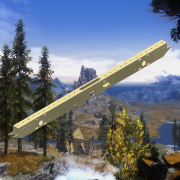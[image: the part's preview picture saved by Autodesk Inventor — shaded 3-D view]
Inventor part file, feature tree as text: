
AUTODESK INVENTOR PART (.ipt)
format: ipt  version: 2015 SP1 (Build 190203100, 203)  size: 1,349,120 bytes
history: native  units: in
note: dims shown in document units (in); Inventor stores cm internally (conversion verified against a paired STEP export)
features: sketch x12, extrude x6, hole x6, reference x6, plane x5, other x2, fillet x1, imported_body x1
ambient origin geometry x8: Origin, YZ Plane, XZ Plane, XY Plane, X Axis, Y Axis, Z Axis, Center Point
bodies: Body1 (feature_tree)
feature tree (39):
  other  "Cut-Extrude2"
  other  "1 x 2 x 0.10 Pre-Drilled Tube Stock (59 length)1"
  plane  "Work Plane2"
  extrude  "Extrusion1"  Depth=99.0in TaperAngle=0.0deg
  extrude  "Extrusion2"  Depth=1.0in
  hole  "Hole1"  [1 undecoded]
  plane  "Work Plane3"
  extrude  "Extrusion3"  TaperAngle=30.0deg  [1 undecoded]
  plane  "Work Plane4"
  extrude  "Extrusion4"  Depth=1.0in
  plane  "Work Plane5"
  extrude  "Extrusion5"  Depth=0.75in
  hole  "Hole2"  [1 undecoded]
  plane  "Work Plane7"
  hole  "Hole3"  [1 undecoded]
  extrude  "Extrusion6"  Depth=4.5in
  hole  "Hole4"  [1 undecoded]
  hole  "Hole5"  [1 undecoded]
  fillet  "Fillet1"  Radius=10.04in
  hole  "Hole6"  [1 undecoded]
  imported_body  "Base1"
  sketch  "Sketch2"  dims[d4=15.5in d5=99.0in d6=0.0in]
  sketch  "Sketch3"  dims[d7=1.0in d8=1.0in]
  sketch  "Sketch4"  dims[d9=30.0deg d10=1.0in]
  sketch  "Sketch5"  dims[d11=1.0in d12=30.0deg]
  sketch  "Sketch6"  dims[d13=1.0in d14=0.0in d16=0.625in]
  sketch  "Sketch7"  dims[d17=15.5in d20=0.75in]
  sketch  "Sketch8"  dims[d21=0.75in]
  sketch  "Sketch10"  dims[d22=0.875in d23=0.75in d24=0.119in d25=0.25in d26=0.563in d27=1.0in d28=0.8108in d29=0.5in]
  sketch  "Sketch11"  dims[d30=3.75in d31=1.0in d32=0.0in]
  sketch  "Sketch12"  dims[d33=0.6in d34=4.5in]
  reference  "Reference1"
  reference  "Reference2"
  sketch  "Sketch13"  dims[d35=1.0in d36=0.0in d37=0.3in]
  reference  "Reference3"
  reference  "Reference4"
  sketch  "Sketch14"  dims[d38=1.0in d39=0.0in d40=10.04in d41=10.04in d42=1.4in d43=0.75in d44=0.375in d45=0.25in d46=0.5635in d47=1.0in d48=0.8108in d49=0.266in d50=0.75in d51=0.507in d52=0.25in d53=0.5635in d54=1.0in d55=0.8108in d56=0.375in d57=0.201in d58=0.201in d59=0.375in d60=0.201in d61=0.375in d62=0.201in d63=0.375in d64=0.201in d65=0.375in d66=0.7874in d68=1.548in d69=0.7874in d71=1.542in d75=1.0in d76=0.0in d77=0.163in d78=0.75in d79=0.507in d80=0.25in d81=0.5635in d82=1.0in d83=0.8108in d85=1.5in d86=0.44in d87=0.44in d88=0.159in d89=0.75in d90=0.375in d91=0.25in d92=0.5635in d93=1.0in d94=0.8108in d95=1.5in d96=0.125in d97=0.177in d98=0.75in d99=0.375in d100=0.25in d101=0.5635in d102=1.0in d103=0.8108in]
  reference  "Reference5"
  reference  "Reference6"
note: 7 required parameter values undecoded (feature->parameter linkage not recoverable at this tier; creation-order binding heuristic only, values carry confidence <= 0.55)
